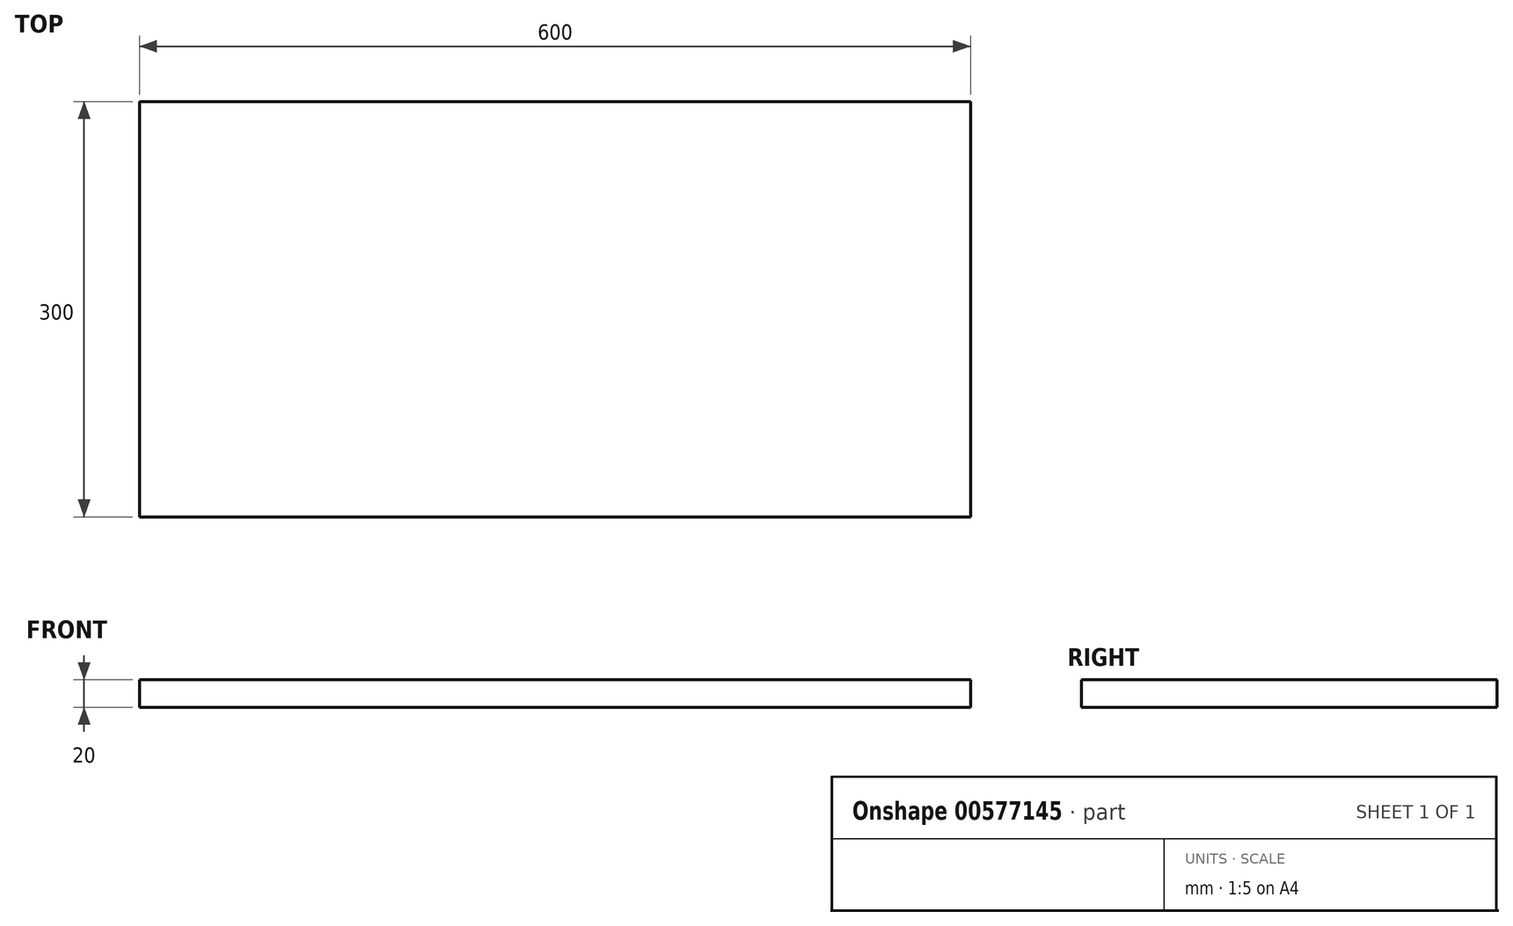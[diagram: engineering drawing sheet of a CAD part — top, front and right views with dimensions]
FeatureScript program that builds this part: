
annotation { "Feature Type Name" : "Feature", "Feature Type Description" : "" }
export const myFeature = defineFeature(function(context is Context, id is Id, definition is map)
    precondition{}
    {
        {
            var Q0;
            Q0=qCreatedBy(makeId("Top.planeOp"),FACE);
            var sketch = newSketch(context, id + "F0", { "sketchPlane" : qUnion([Q0])});
            skLineSegment(sketch, "E0.bottom", {"start": v(-300, 150) * mm, "end": v(300, 150) * mm});
            skLineSegment(sketch, "E0.top", {"start": v(-300, -150) * mm, "end": v(300, -150) * mm});
            skLineSegment(sketch, "E0.left", {"start": v(-300, 150) * mm, "end": v(-300, -150) * mm});
            skLineSegment(sketch, "E0.right", {"start": v(300, 150) * mm, "end": v(300, -150) * mm});
            skPoint(sketch, "E0.middle", {"position": v(0, 0) * mm});
            skSolve(sketch);
        }
        {
            var Q0;
            Q0 = qSketchRegion(id + "F0", true);
            extrude(context, id + "F1", {"entities" : qUnion([Q0]), "depth" : 20 * mm, "offsetDistance" : 25 * mm});
        }
    });
